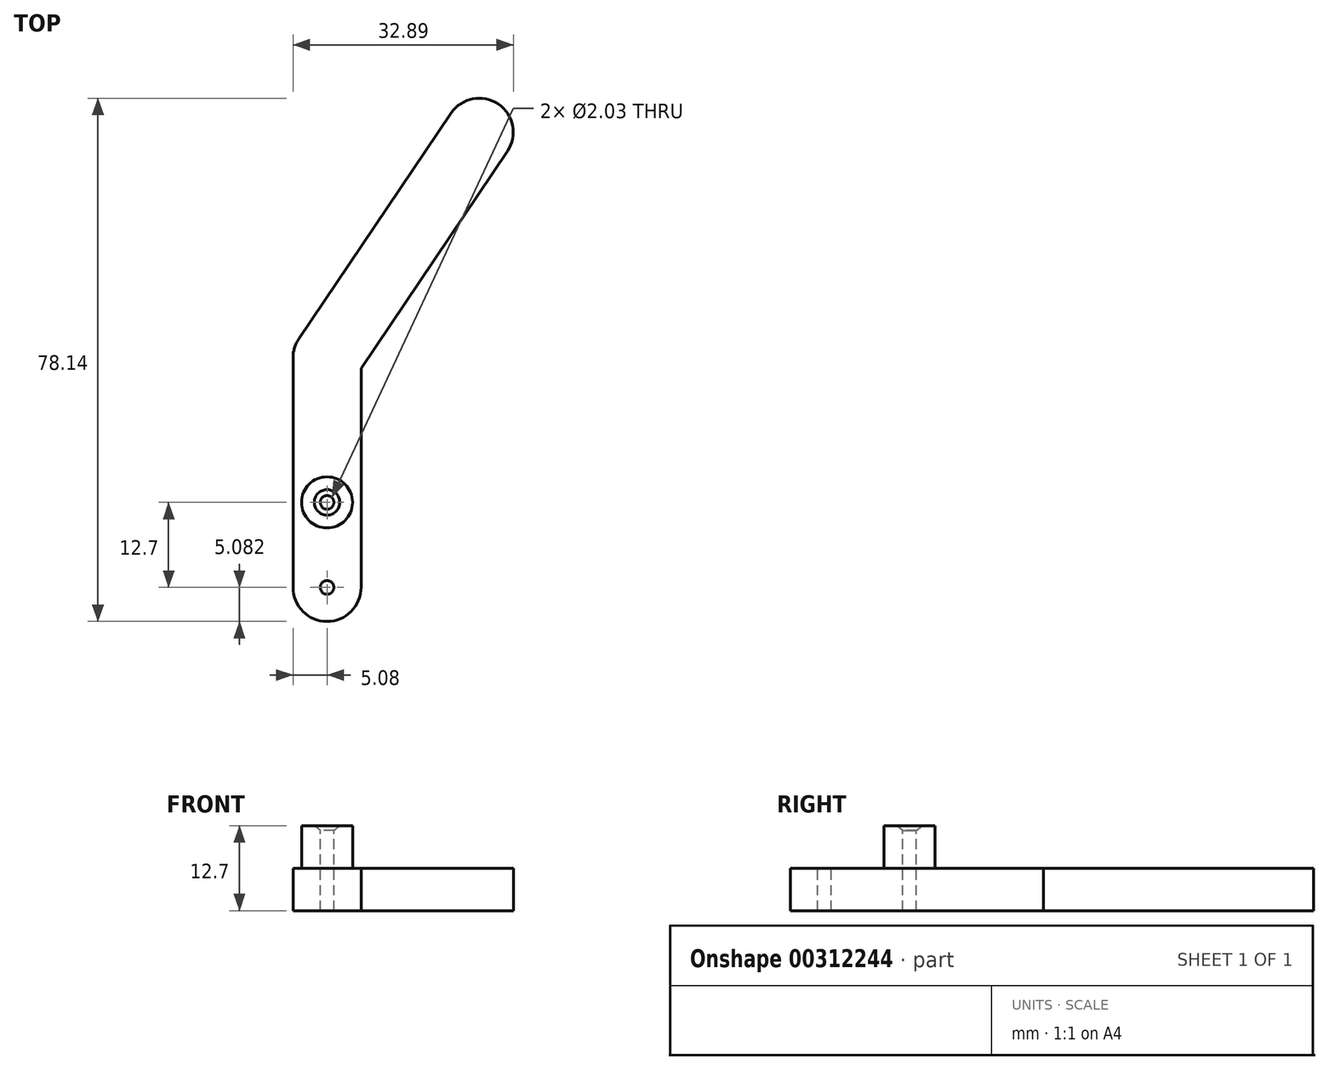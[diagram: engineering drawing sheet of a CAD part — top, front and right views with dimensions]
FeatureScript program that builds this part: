
annotation { "Feature Type Name" : "Feature", "Feature Type Description" : "" }
export const myFeature = defineFeature(function(context is Context, id is Id, definition is map)
    precondition{}
    {
        {
            var Q0;
            Q0=qCreatedBy(makeId("Top.planeOp"),FACE);
            var sketch = newSketch(context, id + "F0", { "sketchPlane" : qUnion([Q0])});
            skLineSegment(sketch, "E0", {"start": v(0, -39.62) * mm, "end": v(0, -26.92) * mm});
            skLineSegment(sketch, "E1", {"start": v(0, -26.92) * mm, "end": v(0, -5.33) * mm});
            skLineSegment(sketch, "E2", {"start": v(0, -5.33) * mm, "end": v(22.73, 28.36) * mm});
            skArc(sketch, "E3.0.startCap", {"start": v(4.21, -8.17) * mm, "mid": v(-2.84, -9.54) * mm, "end": v(-4.21, -2.49) * mm});
            skArc(sketch, "E3.0.endCap", {"start": v(18.51, 31.2) * mm, "mid": v(25.57, 32.58) * mm, "end": v(26.94, 25.52) * mm});
            skLineSegment(sketch, "E3.0.left", {"start": v(-4.21, -2.49) * mm, "end": v(18.51, 31.2) * mm});
            skLineSegment(sketch, "E3.0.right", {"start": v(4.21, -8.17) * mm, "end": v(26.94, 25.52) * mm});
            skArc(sketch, "E3.1.startCap", {"start": v(5.08, -26.92) * mm, "mid": v(0, -32) * mm, "end": v(-5.08, -26.92) * mm});
            skArc(sketch, "E3.1.endCap", {"start": v(-5.08, -5.33) * mm, "mid": v(0, -0.25) * mm, "end": v(5.08, -5.33) * mm});
            skLineSegment(sketch, "E3.1.left", {"start": v(-5.08, -26.92) * mm, "end": v(-5.08, -5.33) * mm});
            skLineSegment(sketch, "E3.1.right", {"start": v(5.08, -26.92) * mm, "end": v(5.08, -5.33) * mm});
            skArc(sketch, "E3.2.startCap", {"start": v(5.08, -39.62) * mm, "mid": v(0, -44.7) * mm, "end": v(-5.08, -39.62) * mm});
            skArc(sketch, "E3.2.endCap", {"start": v(-5.08, -26.92) * mm, "mid": v(0, -21.84) * mm, "end": v(5.08, -26.92) * mm});
            skLineSegment(sketch, "E3.2.left", {"start": v(-5.08, -39.62) * mm, "end": v(-5.08, -26.92) * mm});
            skLineSegment(sketch, "E3.2.right", {"start": v(5.08, -39.62) * mm, "end": v(5.08, -26.92) * mm});
            skSolve(sketch);
        }
        {
            var Q0;
            Q0 = qSketchRegion(id + "F0", true);
            extrude(context, id + "F1", {"entities" : qUnion([Q0]), "depth" : 6.35 * mm});
        }
        {
            var Q0;
            Q0=makeQuery(id+"F1.opExtrude","CAP_FACE",FACE,{"disambiguationData":[OSD([sQuery(id+"F0.wireOp",EDGE,"E3.0.endCap"),sQuery(id+"F0.wireOp",EDGE,"E3.0.left"),sQuery(id+"F0.wireOp",EDGE,"E3.0.right"),sQuery(id+"F0.wireOp",EDGE,"E3.1.endCap"),sQuery(id+"F0.wireOp",EDGE,"E3.1.left"),sQuery(id+"F0.wireOp",EDGE,"E3.1.right"),sQuery(id+"F0.wireOp",EDGE,"E3.2.startCap"),sQuery(id+"F0.wireOp",EDGE,"E3.2.left"),sQuery(id+"F0.wireOp",EDGE,"E3.2.right")])],"isStart":false});
            var sketch = newSketch(context, id + "F2", { "sketchPlane" : qUnion([Q0])});
            skCircle(sketch, "E4", {"center": v(0, -26.92) * mm, "radius": 3.81 * mm});
            skSolve(sketch);
        }
        {
            var Q0;
            Q0 = qSketchRegion(id + "F2", true);
            extrude(context, id + "F3", {"entities" : qUnion([Q0]), "operationType" : NewBodyOperationType.ADD, "depth" : 6.35 * mm});
        }
        {
            var Q0;
            Q0=makeQuery(id+"F3.opExtrude","CAP_FACE",FACE,{"disambiguationData":[OSD([sQuery(id+"F2.wireOp",EDGE,"E4")])],"isStart":false});
            var sketch = newSketch(context, id + "F4", { "sketchPlane" : qUnion([Q0])});
            skPoint(sketch, "E5", {"position": v(0, -26.92) * mm});
            skSolve(sketch);
        }
        {
            var Q0;
            Q0=sQuery(id+"F4.wireOp",VERTEX,"E5");
            var Q1;
            Q1=makeQuery(id+"F1.opExtrude","SWEPT_BODY",BODY,{"disambiguationData":[OSD([sQuery(id+"F0.wireOp",EDGE,"E3.0.endCap"),sQuery(id+"F0.wireOp",EDGE,"E3.0.left"),sQuery(id+"F0.wireOp",EDGE,"E3.0.right"),sQuery(id+"F0.wireOp",EDGE,"E3.1.endCap"),sQuery(id+"F0.wireOp",EDGE,"E3.1.left"),sQuery(id+"F0.wireOp",EDGE,"E3.1.right"),sQuery(id+"F0.wireOp",EDGE,"E3.2.startCap"),sQuery(id+"F0.wireOp",EDGE,"E3.2.left"),sQuery(id+"F0.wireOp",EDGE,"E3.2.right")])]});
            hole(context, id + "F5", {"style" : HoleStyle.C_SINK, "endStyle" : HoleEndStyle.THROUGH, "holeDiameter" : 2.03 * mm, "cSinkDiameter" : 3.8 * mm, "cSinkAngle" : 100 * degree, "tappedDepth" : 12.7 * mm, "tapClearance" : 3, "startFromSketch" : true, "locations" : qUnion([Q0]), "scope" : qUnion([Q1])});
        }
        {
            var Q0;
            Q0=makeQuery(id+"F1.opExtrude","CAP_FACE",FACE,{"disambiguationData":[OSD([sQuery(id+"F0.wireOp",EDGE,"E3.0.endCap"),sQuery(id+"F0.wireOp",EDGE,"E3.0.left"),sQuery(id+"F0.wireOp",EDGE,"E3.0.right"),sQuery(id+"F0.wireOp",EDGE,"E3.1.endCap"),sQuery(id+"F0.wireOp",EDGE,"E3.1.left"),sQuery(id+"F0.wireOp",EDGE,"E3.1.right"),sQuery(id+"F0.wireOp",EDGE,"E3.2.startCap"),sQuery(id+"F0.wireOp",EDGE,"E3.2.left"),sQuery(id+"F0.wireOp",EDGE,"E3.2.right")])],"isStart":false});
            var sketch = newSketch(context, id + "F6", { "sketchPlane" : qUnion([Q0])});
            skPoint(sketch, "E6", {"position": v(0, -39.62) * mm});
            skSolve(sketch);
        }
        {
            var Q0;
            Q0=sQuery(id+"F6.wireOp",VERTEX,"E6");
            var Q1;
            Q1=makeQuery(id+"F1.opExtrude","SWEPT_BODY",BODY,{"disambiguationData":[OSD([sQuery(id+"F0.wireOp",EDGE,"E3.0.endCap"),sQuery(id+"F0.wireOp",EDGE,"E3.0.left"),sQuery(id+"F0.wireOp",EDGE,"E3.0.right"),sQuery(id+"F0.wireOp",EDGE,"E3.1.endCap"),sQuery(id+"F0.wireOp",EDGE,"E3.1.left"),sQuery(id+"F0.wireOp",EDGE,"E3.1.right"),sQuery(id+"F0.wireOp",EDGE,"E3.2.startCap"),sQuery(id+"F0.wireOp",EDGE,"E3.2.left"),sQuery(id+"F0.wireOp",EDGE,"E3.2.right")])]});
            hole(context, id + "F7", {"style" : HoleStyle.SIMPLE, "endStyle" : HoleEndStyle.THROUGH, "holeDiameter" : 2.03 * mm, "tappedDepth" : 12.7 * mm, "tapClearance" : 3, "startFromSketch" : true, "locations" : qUnion([Q0]), "scope" : qUnion([Q1])});
        }
    });
